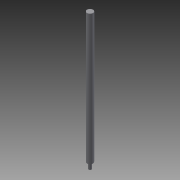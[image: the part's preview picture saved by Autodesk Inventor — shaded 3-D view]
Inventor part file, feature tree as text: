
AUTODESK INVENTOR PART (.ipt)
format: ipt  version: 2013 (Build 170138000, 138)  size: 69,120 bytes
history: native  units: mm
features: extrude x2, sketch x2
ambient origin geometry x8: Origin, YZ Plane, XZ Plane, XY Plane, X Axis, Y Axis, Z Axis, Center Point
bodies: Solid1 (feature_tree)
feature tree (4):
  extrude  "Extrusion1"  Depth=10.0mm TaperAngle=0.0deg
  extrude  "Extrusion2"  Depth=220.0mm TaperAngle=0.0deg
  sketch  "Sketch1"  dims[d0=5.0mm d2=10.0mm d3=0.0mm]
  sketch  "Sketch2"  dims[d4=10.0mm d6=220.0mm d7=0.0mm]
